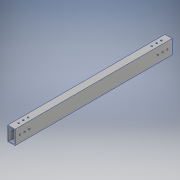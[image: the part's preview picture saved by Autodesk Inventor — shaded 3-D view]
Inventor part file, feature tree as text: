
AUTODESK INVENTOR PART (.ipt)
format: ipt  version: 2019 (Build 230136000, 136)  size: 167,936 bytes
history: native  units: mm
features: sketch x4, extrude x2, hole x2, other x1
ambient origin geometry x8: Origin, YZ Plane, XZ Plane, XY Plane, X Axis, Y Axis, Z Axis, Center Point
bodies: Body1 (feature_tree)
feature tree (9):
  other  "ソリッド1"
  extrude  "押し出し1"  Depth=15.0mm
  hole  "穴1"  [1 undecoded]
  hole  "穴2"  [1 undecoded]
  extrude  "押し出し2"  Depth=3.0mm
  sketch  "スケッチ1"
  sketch  "スケッチ2"
  sketch  "スケッチ3"
  sketch  "スケッチ4"
note: 2 required parameter values undecoded (feature->parameter linkage not recoverable at this tier; creation-order binding heuristic only, values carry confidence <= 0.55)
